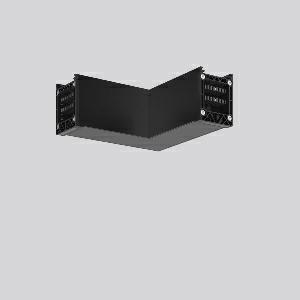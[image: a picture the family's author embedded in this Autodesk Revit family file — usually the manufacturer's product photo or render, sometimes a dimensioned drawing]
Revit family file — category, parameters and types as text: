
# Revit family: linedo_l-verbindung_982773_003_1_3b48
name_source: partatom
category: Lighting Fixtures
units: mm (PartAtom-declared; Revit-internal decimal feet)

## family parameters
Cut with Voids When Loaded = No
Host = Face
Light Source = No
Part Type = Normal
Room Calculation Point = No
Round Connector Dimension = Use Diameter
Shared = No

## types (1)
- LINEDO L-Verbindung
    Apparent Load = 0 VA
    Default Elevation = 1800 mm
    Description = Series: LINEDO
L-connector, 14-pole, connection socket / socket. Housing: extruded aluminium profile, powder-coated. Cover made of plastic, surface like housing. LINEDO plug system, plastic, black. Easy connection for rigid or flexible wires. 2 membrane cable entries (M25). Suitable for power supply in 7-pole version. Ready prewired. Colour-coded individual cables enable easy electromechanical separation.
Colour: jet black (RAL 9005)
Length: 185 mm
Width: 185 mm
Height: 76 mm
Weight: 730 g
    Height = 76 mm
    Lamp = 0 x
    Length = 185 mm
    Luminous efficacy = 0 lm/W
    Manufacturer = RZB
    ModVariant = No
    Model = 982773.003.1
    Mounting Place = Ceiling
    Mounting Type = Surface mounted
    Number of Poles = 1
    OnlyDefault = Yes
    Power Factor = 1
    Product Name = LINEDO L-Verbindung
    Product group = Surface mounted continuous line luminaire system
    ProductGroupID = 310
    Protection Class = Protection class I
    Protection Degree = Degree of protection
    RLX_Detail_Level = 1
    RLX_Emergency_Light_Flux = 0 lm
    RLX_Emergency_Type = 0
    RLX_Emergency_Type_DB = No
    RlxData = <blob elided: 19029 chars, md5=358da9ab>
    Standby Power = 0 W
    System Light Flux = 0 lm
    System Power = 0 W
    Type Comments = Product without accessories
    Type Image = 982773.003.1.jpg
    URL = http://relux.com
    VarID = ---
    Voltage = 0 V
    Weight = 0.00 kg
    Width = 185 mm

## geometry (parser evidence)
native form markers: Blend x4, Sweep x12
no freeform markers — native parametric forms only
